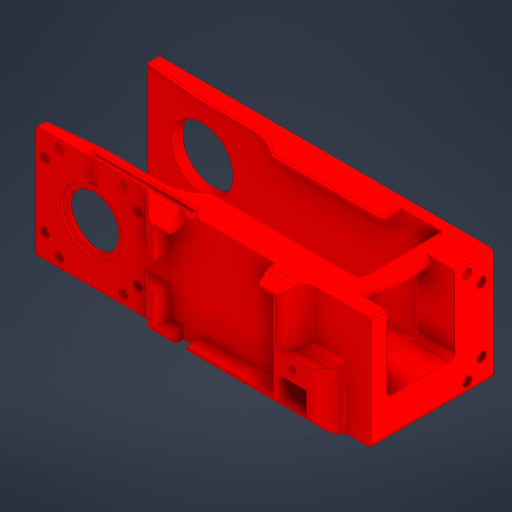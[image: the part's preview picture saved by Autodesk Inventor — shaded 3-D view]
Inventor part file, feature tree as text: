
AUTODESK INVENTOR PART (.ipt)
format: ipt  version: 2023.4 (Build 274418000, 418)  size: 1,384,448 bytes
history: native  units: mm
features: extrude x19, projected_geometry x14, sketch x11, reference x10, plane x5, fillet x4, chamfer x3, other x3, mirror x1
ambient origin geometry x8: Origin, YZ Plane, XZ Plane, XY Plane, X Axis, Y Axis, Z Axis, Center Point
bodies: Solid1 (feature_tree)
feature tree (70):
  extrude  "Extrusion1"  Depth=10.0mm
  plane  "Work Plane1"
  plane  "Work Plane2"
  plane  "Work Plane3"
  extrude  "Extrusion2"  Depth=2.0mm TaperAngle=0.0deg
  mirror  "Mirror1"
  extrude  "Extrusion3"  Depth=50.0mm
  extrude  "Extrusion4"  Depth=50.0mm
  sketch  "Sketch5"  dims[d23=49.9mm d24=5.0mm]
  extrude  "Extrusion5"  Depth=5.0mm
  extrude  "Extrusion6"  Depth=50.0mm TaperAngle=0.0deg
  extrude  "Extrusion7"  Depth=2.5mm
  extrude  "Extrusion8"  Depth=12.15mm
  chamfer  "Chamfer1"  Distance=9.5mm
  chamfer  "Chamfer2"  Distance=9.9675mm
  extrude  "Extrusion9"  Depth=10.0mm
  fillet  "Fillet1"  Radius=27.5mm
  plane  "Work Plane4"
  extrude  "Extrusion10"  Depth=10.0mm TaperAngle=0.0deg
  sketch  "Sketch8"  dims[d34=33.5mm d35=12.15mm]
  extrude  "Extrusion11"  Depth=10.0mm TaperAngle=0.0deg
  extrude  "Extrusion12"  Depth=10.0mm TaperAngle=45.0deg
  extrude  "Extrusion13"  Depth=10.0mm TaperAngle=45.0deg
  fillet  "Fillet2"  Radius=10.0mm
  sketch  "Sketch10"  dims[d37=5.5mm]
  extrude  "Extrusion14"  Depth=10.0mm
  extrude  "Extrusion15"  Depth=10.0mm
  extrude  "Extrusion16"  Depth=10.0mm
  plane  "Work Plane5"
  extrude  "Extrusion18"  Depth=10.0mm
  extrude  "Extrusion19"  Depth=10.0mm
  extrude  "Extrusion20"  Depth=10.0mm TaperAngle=0.0deg
  chamfer  "Chamfer3"  Distance=2.5mm
  fillet  "Fillet3"  Radius=8.5mm
  fillet  "Fillet4"  Radius=8.5mm
  sketch  "Sketch1"  dims[d0=30.0mm d2=50.0mm d3=10.0mm d5=10.0mm d7=1.0mm]
  reference  "Reference1"
  reference  "Reference2"
  reference  "Reference3"
  reference  "Reference4"
  reference  "Reference5"
  reference  "Reference6"
  reference  "Reference7"
  reference  "Reference8"
  reference  "Reference9"
  sketch  "Sketch2"  dims[d8=50.0mm d9=0.0mm d17=2.0mm d18=0.0mm]
  reference  "Reference10"
  sketch  "Sketch3"  dims[d19=49.9mm d20=50.0mm]
  sketch  "Sketch4"  dims[d21=50.0mm d22=50.0mm]
  projected_geometry  "Projected Loop3"
  projected_geometry  "Projected Loop12"
  sketch  "Sketch6"  dims[d25=5.0mm d26=50.0mm d27=0.0mm]
  projected_geometry  "Projected Loop14"
  projected_geometry  "Projected Loop15"
  projected_geometry  "Projected Loop16"
  sketch  "Sketch7"  dims[d29=150.0mm d30=75.0mm d31=0.0mm d32=0.0mm d33=2.5mm]
  projected_geometry  "Projected Loop17"
  projected_geometry  "Projected Loop18"
  projected_geometry  "Projected Loop19"
  sketch  "Sketch9"  dims[d36=12.5mm]
  projected_geometry  "Projected Loop20"
  sketch  "Sketch11"  dims[d38=2.5mm d39=9.5mm d40=0.0mm d41=9.9675mm d42=0.0mm d43=49.8mm d44=27.5mm d45=10.0mm d46=0.0mm d47=3.0mm d48=0.0mm d49=9.5mm d50=2.0mm d51=45.0deg d52=4.25mm d53=2.0mm d54=45.0deg d55=10.0mm d56=12.0mm d57=8.0mm d58=0.375mm d59=0.375mm d60=0.375mm d61=9.9675mm d62=0.0mm d63=2.5mm d64=8.5mm d65=8.5mm d66=-1.25mm d67=10.0mm d68=0.0mm d69=5.0mm d71=9.5mm d72=10.75mm d73=10.0mm d74=0.0mm d75=10.0mm d76=0.0mm d77=2.5mm d78=2.0mm d80=2.0mm d81=2.0mm d83=2.0mm d84=2.0mm d85=2.0mm d86=2.5mm d87=0.0mm d88=0.5mm d89=0.0mm d90=2.0mm d91=0.0mm d93=2.0mm d94=0.0mm d95=2.0mm d96=0.0mm d97=3.75mm d105=53.25mm d106=39.0mm d107=2.5mm d108=40.0mm d109=12.5mm d110=5.5mm d111=9.0mm d114=12.0mm d115=0.0mm d119=49.8mm d120=49.8mm d121=8.0mm d122=10.5mm d123=10.5mm d124=4.1mm d125=4.15mm d130=7.85mm d131=7.85mm d132=5.5mm d133=5.5mm d135=2.0mm d136=0.0mm d138=7.5mm d139=6.25mm d140=40.0mm d142=360.0deg d144=2.875mm d145=23.251089mm d146=32.5mm d147=30.75mm d148=3.0mm d149=1.25mm d150=3.0mm d151=0.875mm d154=1.25mm d155=0.0mm d156=1.75mm d157=0.0mm d158=1.25mm d159=135.0deg d160=2.0mm d161=1.75mm d162=0.0mm d163=1.75mm d164=2.0mm d165=45.0deg d167=0.0575mm d169=0.0575mm d170=40.0mm d172=360.0deg d174=30.0mm d176=50.0mm d177=10.0mm d179=10.0mm d181=2.5mm d182=2.0mm d116=0.5mm d117=0.872665mm d141=0.0mm d152=0.0mm d153=0.5mm d168=0.0mm]
  projected_geometry  "Projected Loop27"
  projected_geometry  "Projected Loop28"
  projected_geometry  "Projected Loop29"
  projected_geometry  "Projected Loop30"
  projected_geometry  "Projected Loop31"
  parser-record x1  (decoder bookkeeping rows leaked as tree rows — omitted from the tree; the rows remain in map.json)
  other  "Cube 1x1 V5.iam"
  other  "Cube 1x1 Top V5:1"
note: 1 file-system path scrubbed to <path> (originals preserved in map.json)
